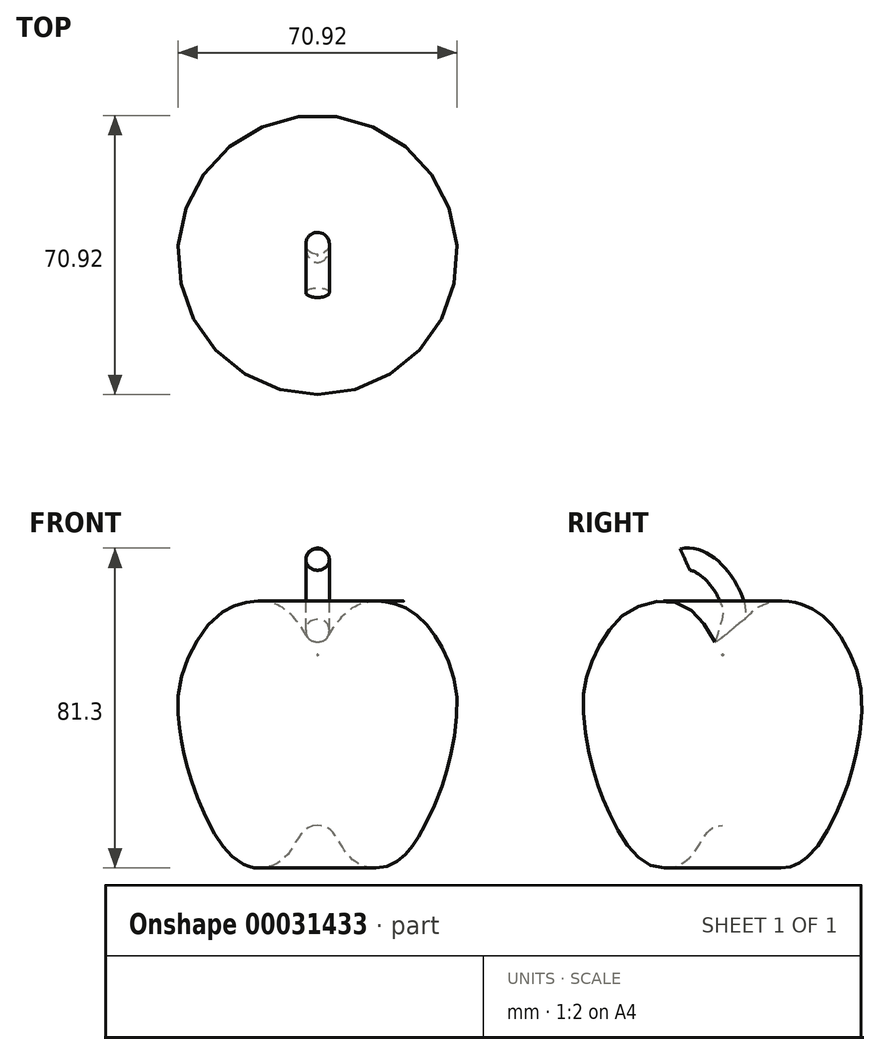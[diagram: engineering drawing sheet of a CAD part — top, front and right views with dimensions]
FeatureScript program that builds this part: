
annotation { "Feature Type Name" : "Feature", "Feature Type Description" : "" }
export const myFeature = defineFeature(function(context is Context, id is Id, definition is map)
    precondition{}
    {
        {
            var Q0;
            Q0=qCreatedBy(makeId("Right.planeOp"),FACE);
            var sketch = newSketch(context, id + "F0", { "sketchPlane" : qUnion([Q0])});
            skLineSegment(sketch, "E0", {"start": v(0, 37.78) * mm, "end": v(0, -5.27) * mm});
            skFitSpline(sketch, "E1", {"points": [v(0, 37.78) * mm, v(-10.16, 50.72) * mm, v(-23.98, 49.04) * mm, v(-32.63, 37.78) * mm, v(-35.46, 25.8) * mm, v(-33.06, 9.43) * mm, v(-29.77, 0) * mm, v(-23.32, -11.5) * mm, v(-15.78, -16.07) * mm, v(-7.64, -12.73) * mm, v(0, -5.27) * mm], "startDerivative": vector(-73.05, 140.04) * mm, "endDerivative": vector(137.3, 0) * mm});
            skSolve(sketch);
        }
        {
            var Q0;
            Q0=makeQuery(id+"F0.imprint","IMPRINT",FACE,{"disambiguationData":[TD([[makeQuery(id+"F0.imprint","IMPRINT",EDGE,{"derivedFrom":sQuery(id+"F0.wireOp",EDGE,"E0")}),-1.0]])]});
            var Q1;
            Q1=sQuery(id+"F0.wireOp",EDGE,"E0");
            revolve(context, id + "F1", {"entities" : qUnion([Q0]), "axis" : qUnion([Q1]), "revolveType" : RevolveType.FULL});
        }
        {
            var Q0;
            Q0=qCreatedBy(makeId("Top.planeOp"),FACE);
            cPlane(context, id + "F2", {"entities" : qUnion([Q0]), "cplaneType" : CPlaneType.OFFSET, "offset" : 38.1 * mm, "width" : 152.4 * mm, "height" : 152.4 * mm});
        }
        {
            var Q0;
            Q0=qCreatedBy(id+"F2.planeOp",FACE);
            var sketch = newSketch(context, id + "F3", { "sketchPlane" : qUnion([Q0])});
            skCircle(sketch, "E2", {"center": v(0, 0) * mm, "radius": 2.98 * mm});
            skSolve(sketch);
        }
        {
            var Q0;
            Q0=qCreatedBy(makeId("Right.planeOp"),FACE);
            var sketch = newSketch(context, id + "F4", { "sketchPlane" : qUnion([Q0])});
            skFitSpline(sketch, "E3", {"points": [v(0, 38.1) * mm, v(2.11, 52.38) * mm, v(-9.55, 62.26) * mm], "startDerivative": vector(16.25, 49.37) * mm, "endDerivative": vector(-31.32, -3.4) * mm});
            skSolve(sketch);
        }
        {
            var Q0;
            Q0=makeQuery(id+"F3.imprint","IMPRINT",FACE,{"disambiguationData":[TD([[makeQuery(id+"F3.imprint","IMPRINT",EDGE,{"derivedFrom":sQuery(id+"F3.wireOp",EDGE,"E2")}),1.0]])]});
            var Q1;
            Q1=sQuery(id+"F4.wireOp",EDGE,"E3");
            sweep(context, id + "F5", {"operationType" : NewBodyOperationType.ADD, "profiles" : qUnion([Q0]), "path" : qUnion([Q1])});
        }
    });
